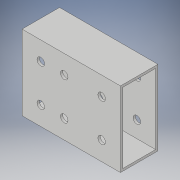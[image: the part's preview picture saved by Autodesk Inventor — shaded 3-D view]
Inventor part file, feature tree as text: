
AUTODESK INVENTOR PART (.ipt)
format: ipt  version: 2018 (Build 220112000, 112)  size: 130,048 bytes
history: native  units: in
note: dims shown in document units (in); Inventor stores cm internally (conversion verified against a paired STEP export)
features: hole x6, extrude x1, shell x1, sketch x1
ambient origin geometry x8: Origin, YZ Plane, XZ Plane, XY Plane, X Axis, Y Axis, Z Axis, Center Point
bodies: Solid1 (feature_tree)
feature tree (9):
  extrude  "Extrusion1"  Depth=1.0in
  shell  "Shell1"  Thickness=2.625in
  hole  "Hole1"  [1 undecoded]
  hole  "Hole2"  [1 undecoded]
  hole  "Hole3"  [1 undecoded]
  hole  "Hole4"  [1 undecoded]
  hole  "Hole5"  [1 undecoded]
  hole  "Hole6"  [1 undecoded]
  sketch  "Sketch1"  dims[d0=2.0in d1=1.0in d2=2.625in d3=0.0in d4=0.0625in d5=0.5in d6=0.5in d7=0.2031in d8=0.75in d9=0.375in d10=0.25in d11=0.5635in d12=1.0in d13=0.8108in d14=0.5in d15=0.5in d16=0.2031in d17=0.75in d18=0.375in d19=0.25in d20=0.5635in d21=1.0in d22=0.8108in d23=0.5in d24=0.5in d25=0.2031in d26=0.75in d27=0.375in d28=0.25in d29=0.5635in d30=1.0in d31=0.8108in d32=0.5in d33=0.5in d34=0.2031in d35=0.75in d36=0.375in d37=0.25in d38=0.5635in d39=1.0in d40=0.8108in d41=0.5in d42=1.5in d43=0.2031in d44=0.75in d45=0.375in d46=0.25in d47=0.5635in d48=1.0in d49=0.8108in d50=0.5in d51=1.5in d52=0.2031in d53=0.75in d54=0.375in d55=0.25in d56=0.5635in d57=1.0in d58=0.8108in]
note: 6 required parameter values undecoded (feature->parameter linkage not recoverable at this tier; creation-order binding heuristic only, values carry confidence <= 0.55)
